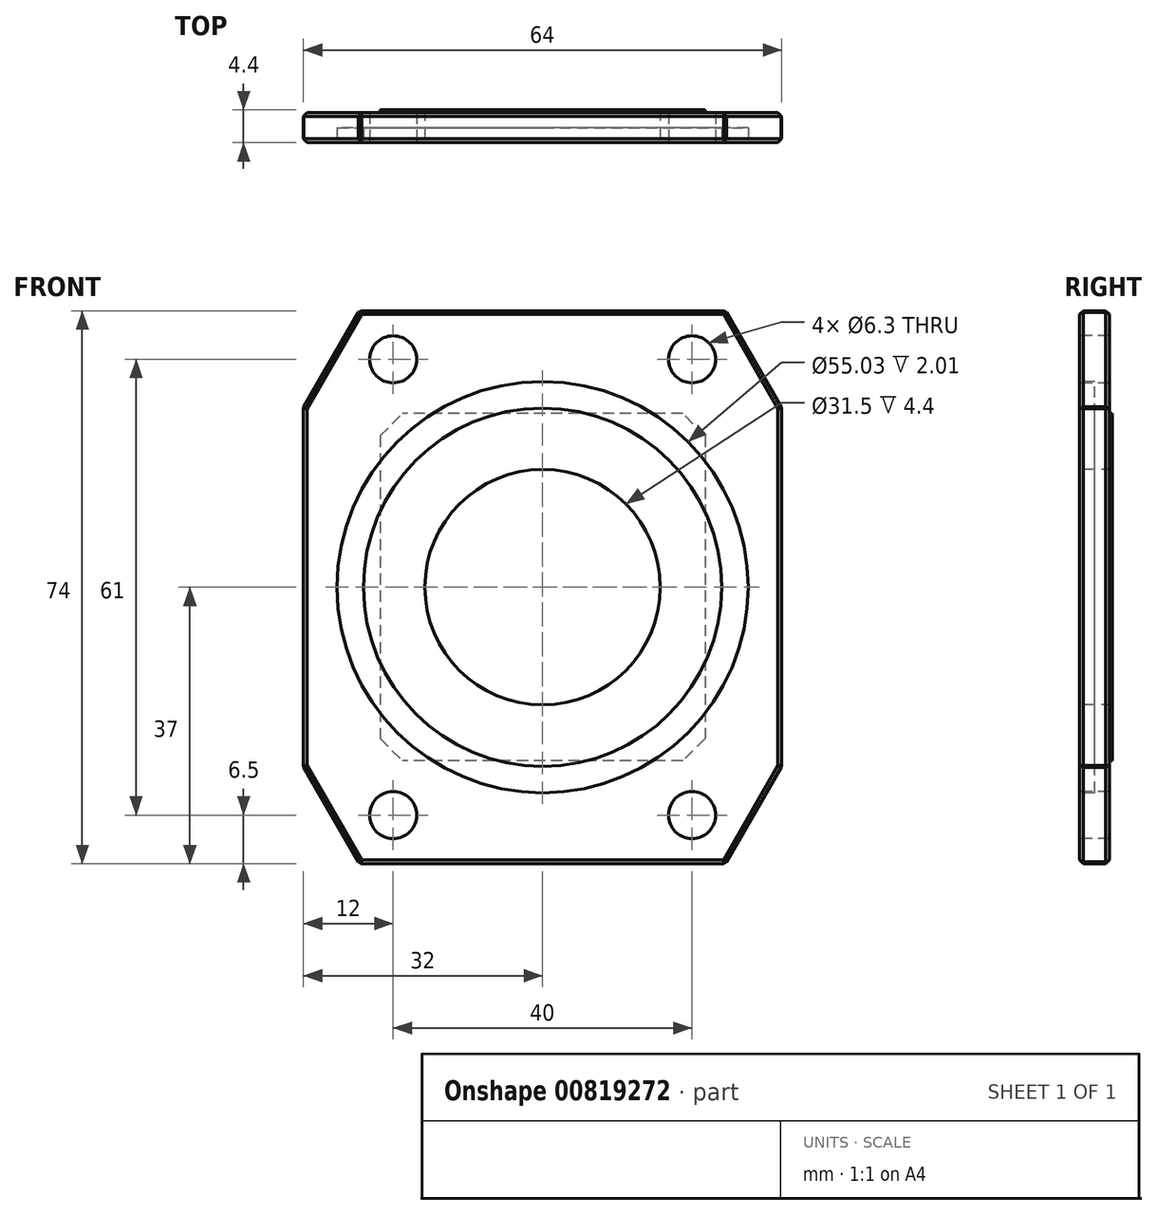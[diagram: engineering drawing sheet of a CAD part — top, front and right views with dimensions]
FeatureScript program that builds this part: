
annotation { "Feature Type Name" : "Feature", "Feature Type Description" : "" }
export const myFeature = defineFeature(function(context is Context, id is Id, definition is map)
    precondition{}
    {
        {
            var Q0;
            Q0=qCreatedBy(makeId("Front.planeOp"),FACE);
            var sketch = newSketch(context, id + "F0", { "sketchPlane" : qUnion([Q0])});
            skLineSegment(sketch, "E0", {"start": v(-32, -24) * mm, "end": v(-32, 24) * mm});
            skLineSegment(sketch, "E1", {"start": v(-32, 24) * mm, "end": v(-24.5, 37) * mm});
            skLineSegment(sketch, "E2", {"start": v(-24.5, 37) * mm, "end": v(24.5, 37) * mm});
            skLineSegment(sketch, "E3", {"start": v(24.5, 37) * mm, "end": v(32, 24) * mm});
            skLineSegment(sketch, "E4", {"start": v(32, 24) * mm, "end": v(32, -24) * mm});
            skLineSegment(sketch, "E5", {"start": v(32, -24) * mm, "end": v(24.5, -37) * mm});
            skLineSegment(sketch, "E6", {"start": v(24.5, -37) * mm, "end": v(-24.5, -37) * mm});
            skLineSegment(sketch, "E7", {"start": v(-24.5, -37) * mm, "end": v(-32, -24) * mm});
            skPoint(sketch, "E8", {"position": v(-32, 0) * mm});
            skPoint(sketch, "E9", {"position": v(32, 0) * mm});
            skLineSegment(sketch, "E10", {"start": v(-43.5, 0) * mm, "end": v(-20.5, 0) * mm, "construction": true});
            skLineSegment(sketch, "E11", {"start": v(0, 24) * mm, "end": v(0, 50) * mm, "construction": true});
            skPoint(sketch, "E12", {"position": v(0, 37) * mm});
            skSolve(sketch);
        }
        {
            var Q0;
            Q0=makeQuery(id+"F0.imprint","IMPRINT",FACE,{"disambiguationData":[TD([[makeQuery(id+"F0.imprint","IMPRINT",EDGE,{"derivedFrom":sQuery(id+"F0.wireOp",EDGE,"E0")}),-1.0]])]});
            extrude(context, id + "F1", {"entities" : qUnion([Q0]), "depth" : 4 * mm, "offsetDistance" : 25 * mm});
        }
        {
            var Q0;
            Q0=makeQuery(id+"F1.opExtrude","CAP_FACE",FACE,{"disambiguationData":[OSD([sQuery(id+"F0.wireOp",EDGE,"E0"),sQuery(id+"F0.wireOp",EDGE,"E1"),sQuery(id+"F0.wireOp",EDGE,"E2"),sQuery(id+"F0.wireOp",EDGE,"E3"),sQuery(id+"F0.wireOp",EDGE,"E4"),sQuery(id+"F0.wireOp",EDGE,"E5"),sQuery(id+"F0.wireOp",EDGE,"E6"),sQuery(id+"F0.wireOp",EDGE,"E7")])],"isStart":false});
            var sketch = newSketch(context, id + "F2", { "sketchPlane" : qUnion([Q0])});
            skPoint(sketch, "E13", {"position": v(-20, 30.5) * mm});
            skPoint(sketch, "E14.MirrorP", {"position": v(20, 30.5) * mm});
            skPoint(sketch, "E15.MirrorP", {"position": v(-20, -30.5) * mm});
            skPoint(sketch, "E16.MirrorP", {"position": v(20, -30.5) * mm});
            skSolve(sketch);
        }
        {
            var Q0;
            Q0=sQuery(id+"F2.wireOp",VERTEX,"E13");
            var Q1;
            Q1=sQuery(id+"F2.wireOp",VERTEX,"E14.MirrorP");
            var Q2;
            Q2=sQuery(id+"F2.wireOp",VERTEX,"E16.MirrorP");
            var Q3;
            Q3=sQuery(id+"F2.wireOp",VERTEX,"E15.MirrorP");
            var Q4;
            Q4=makeQuery(id+"F1.opExtrude","SWEPT_BODY",BODY,{"disambiguationData":[OSD([sQuery(id+"F0.wireOp",EDGE,"E0"),sQuery(id+"F0.wireOp",EDGE,"E1"),sQuery(id+"F0.wireOp",EDGE,"E2"),sQuery(id+"F0.wireOp",EDGE,"E3"),sQuery(id+"F0.wireOp",EDGE,"E4"),sQuery(id+"F0.wireOp",EDGE,"E5"),sQuery(id+"F0.wireOp",EDGE,"E6"),sQuery(id+"F0.wireOp",EDGE,"E7")])]});
            hole(context, id + "F3", {"style" : HoleStyle.SIMPLE, "endStyle" : HoleEndStyle.THROUGH, "holeDiameter" : 6.3 * mm, "majorDiameter" : 6 * mm, "tappedDepth" : 15 * mm, "tapClearance" : 3, "locations" : qUnion([Q0, Q1, Q2, Q3]), "scope" : qUnion([Q4])});
        }
        {
            var Q0;
            Q0=makeQuery(id+"F1.opExtrude","CAP_FACE",FACE,{"disambiguationData":[OSD([sQuery(id+"F0.wireOp",EDGE,"E0"),sQuery(id+"F0.wireOp",EDGE,"E1"),sQuery(id+"F0.wireOp",EDGE,"E2"),sQuery(id+"F0.wireOp",EDGE,"E3"),sQuery(id+"F0.wireOp",EDGE,"E4"),sQuery(id+"F0.wireOp",EDGE,"E5"),sQuery(id+"F0.wireOp",EDGE,"E6"),sQuery(id+"F0.wireOp",EDGE,"E7")])],"isStart":true});
            var sketch = newSketch(context, id + "F4", { "sketchPlane" : qUnion([Q0])});
            skLineSegment(sketch, "E17.bottom", {"start": v(-21.75, 23.25) * mm, "end": v(21.75, 23.25) * mm});
            skLineSegment(sketch, "E17.top", {"start": v(-21.75, -23.25) * mm, "end": v(21.75, -23.25) * mm});
            skLineSegment(sketch, "E17.left", {"start": v(-21.75, 23.25) * mm, "end": v(-21.75, -23.25) * mm});
            skLineSegment(sketch, "E17.right", {"start": v(21.75, 23.25) * mm, "end": v(21.75, -23.25) * mm});
            skPoint(sketch, "E18", {"position": v(-21.75, 0) * mm});
            skPoint(sketch, "E19", {"position": v(0, 23.25) * mm});
            skLineSegment(sketch, "E20", {"start": v(0, 19.99) * mm, "end": v(0, 26.51) * mm, "construction": true});
            skLineSegment(sketch, "E21", {"start": v(-31.8, 0) * mm, "end": v(-11.7, 0) * mm, "construction": true});
            skSolve(sketch);
        }
        {
            var Q0;
            Q0=makeQuery(id+"F4.imprint","IMPRINT",FACE,{"disambiguationData":[TD([[makeQuery(id+"F4.imprint","IMPRINT",EDGE,{"derivedFrom":sQuery(id+"F4.wireOp",EDGE,"E17.bottom")}),-1.0]])]});
            extrude(context, id + "F5", {"entities" : qUnion([Q0]), "operationType" : NewBodyOperationType.ADD, "depth" : 0.4 * mm, "offsetDistance" : 25 * mm});
        }
        {
            var Q0;
            {var subQ0=sQuery(id+"F0.wireOp",EDGE,"E6");var subQ1=sQuery(id+"F0.wireOp",EDGE,"E7");var subQ2=sQuery(id+"F0.wireOp",EDGE,"E5");var subQ3=sQuery(id+"F0.wireOp",EDGE,"E4");var subQ4=sQuery(id+"F0.wireOp",EDGE,"E0");var subQ5=sQuery(id+"F0.wireOp",EDGE,"E3");var subQ6=sQuery(id+"F0.wireOp",EDGE,"E1");var subQ7=sQuery(id+"F0.wireOp",EDGE,"E2");Q0=makeQuery(id+"FPjBMLfvsBLIMmg_1.boolean.opBoolean","SPLIT",FACE,{"disambiguationData":[TD([makeQuery(id+"F1.opExtrude","SWEPT_FACE",FACE,{"disambiguationData":[OSD([subQ4])]})])],"derivedFrom":makeQuery(id+"F1.opExtrude","CAP_FACE",FACE,{"disambiguationData":[OSD([subQ4,subQ6,subQ7,subQ5,subQ3,subQ2,subQ0,subQ1])],"isStart":false})});}
            var sketch = newSketch(context, id + "F6", { "sketchPlane" : qUnion([Q0])});
            skCircle(sketch, "E22", {"center": v(0, 0) * mm, "radius": 27.52 * mm});
            skCircle(sketch, "E23", {"center": v(0, 0) * mm, "radius": 23.98 * mm});
            skSolve(sketch);
        }
        {
            var Q0;
            Q0=makeQuery(id+"F6.imprint","IMPRINT",FACE,{"disambiguationData":[TD([[makeQuery(id+"F6.imprint","IMPRINT",EDGE,{"derivedFrom":sQuery(id+"F6.wireOp",EDGE,"E22")}),1.0]])]});
            extrude(context, id + "F7", {"entities" : qUnion([Q0]), "operationType" : NewBodyOperationType.REMOVE, "oppositeDirection" : true, "depth" : 2 * mm, "offsetDistance" : 25 * mm});
        }
        {
            var Q0;
            Q0=makeQuery(id+"F7.boolean.opBoolean","SPLIT",FACE,{"disambiguationData":[TD([makeQuery(id+"F7.opExtrude","SWEPT_FACE",FACE,{"disambiguationData":[OSD([sQuery(id+"F6.wireOp",EDGE,"E23")])]})])],"derivedFrom":makeQuery(id+"F1.opExtrude","CAP_FACE",FACE,{"disambiguationData":[OSD([sQuery(id+"F0.wireOp",EDGE,"E0"),sQuery(id+"F0.wireOp",EDGE,"E1"),sQuery(id+"F0.wireOp",EDGE,"E2"),sQuery(id+"F0.wireOp",EDGE,"E3"),sQuery(id+"F0.wireOp",EDGE,"E4"),sQuery(id+"F0.wireOp",EDGE,"E5"),sQuery(id+"F0.wireOp",EDGE,"E6"),sQuery(id+"F0.wireOp",EDGE,"E7")])],"isStart":false})});
            var sketch = newSketch(context, id + "F8", { "sketchPlane" : qUnion([Q0])});
            skCircle(sketch, "E24", {"center": v(0, 0) * mm, "radius": 15.75 * mm});
            skSolve(sketch);
        }
        {
            var Q0;
            Q0=makeQuery(id+"F8.imprint","IMPRINT",FACE,{"disambiguationData":[TD([[makeQuery(id+"F8.imprint","IMPRINT",EDGE,{"derivedFrom":sQuery(id+"F8.wireOp",EDGE,"E24")}),1.0]])]});
            extrude(context, id + "F9", {"entities" : qUnion([Q0]), "operationType" : NewBodyOperationType.REMOVE, "endBound" : BoundingType.THROUGH_ALL, "oppositeDirection" : true, "depth" : 25 * mm, "offsetDistance" : 25 * mm});
        }
        {
            var Q0;
            Q0=makeQuery(id+"F1.opExtrude","SWEPT_FACE",FACE,{"disambiguationData":[OSD([sQuery(id+"F0.wireOp",EDGE,"E2")])]});
            var Q1;
            Q1=makeQuery(id+"F1.opExtrude","SWEPT_FACE",FACE,{"disambiguationData":[OSD([sQuery(id+"F0.wireOp",EDGE,"E1")])]});
            var Q2;
            Q2=makeQuery(id+"F1.opExtrude","SWEPT_FACE",FACE,{"disambiguationData":[OSD([sQuery(id+"F0.wireOp",EDGE,"E0")])]});
            var Q3;
            Q3=makeQuery(id+"F1.opExtrude","SWEPT_FACE",FACE,{"disambiguationData":[OSD([sQuery(id+"F0.wireOp",EDGE,"E7")])]});
            var Q4;
            Q4=makeQuery(id+"F1.opExtrude","SWEPT_FACE",FACE,{"disambiguationData":[OSD([sQuery(id+"F0.wireOp",EDGE,"E6")])]});
            var Q5;
            Q5=makeQuery(id+"F1.opExtrude","SWEPT_FACE",FACE,{"disambiguationData":[OSD([sQuery(id+"F0.wireOp",EDGE,"E4")])]});
            var Q6;
            Q6=makeQuery(id+"F1.opExtrude","SWEPT_FACE",FACE,{"disambiguationData":[OSD([sQuery(id+"F0.wireOp",EDGE,"E3")])]});
            var Q7;
            Q7=makeQuery(id+"F1.opExtrude","SWEPT_FACE",FACE,{"disambiguationData":[OSD([sQuery(id+"F0.wireOp",EDGE,"E5")])]});
            chamfer(context, id + "F10", {"entities" : qUnion([Q0, Q1, Q2, Q3, Q4, Q5, Q6, Q7]), "width" : 0.5 * mm, "tangentPropagation" : true});
        }
        {
            var Q0;
            Q0=makeQuery(id+"F7.boolean.opBoolean","COPY",EDGE,{"derivedFrom":makeQuery(id+"F7.opExtrude","CAP_EDGE",EDGE,{"disambiguationData":[OSD([sQuery(id+"F6.wireOp",EDGE,"E23")])],"isStart":true})});
            var Q1;
            Q1=makeQuery(id+"F7.boolean.opBoolean","COPY",EDGE,{"derivedFrom":makeQuery(id+"F7.opExtrude","CAP_EDGE",EDGE,{"disambiguationData":[OSD([sQuery(id+"F6.wireOp",EDGE,"E22")])],"isStart":true})});
            fillet(context, id + "F11", {"entities" : qUnion([Q0, Q1]), "radius" : 0.2 * mm, "tangentPropagation" : true, "allowEdgeOverflow" : false});
        }
        {
            var Q0;
            Q0=makeQuery(id+"F5.opExtrude","SWEPT_EDGE",EDGE,{"disambiguationData":[OSD([sQuery(id+"F4.wireOp",EDGE,"E17.bottom"),sQuery(id+"F4.wireOp",EDGE,"E17.left")])]});
            var Q1;
            Q1=makeQuery(id+"F5.opExtrude","SWEPT_EDGE",EDGE,{"disambiguationData":[OSD([sQuery(id+"F4.wireOp",EDGE,"E17.bottom"),sQuery(id+"F4.wireOp",EDGE,"E17.right")])]});
            var Q2;
            Q2=makeQuery(id+"F5.opExtrude","SWEPT_EDGE",EDGE,{"disambiguationData":[OSD([sQuery(id+"F4.wireOp",EDGE,"E17.top"),sQuery(id+"F4.wireOp",EDGE,"E17.right")])]});
            var Q3;
            Q3=makeQuery(id+"F5.opExtrude","SWEPT_EDGE",EDGE,{"disambiguationData":[OSD([sQuery(id+"F4.wireOp",EDGE,"E17.top"),sQuery(id+"F4.wireOp",EDGE,"E17.left")])]});
            chamfer(context, id + "F12", {"entities" : qUnion([Q0, Q1, Q2, Q3]), "width" : 3 * mm, "tangentPropagation" : true});
        }
    });
